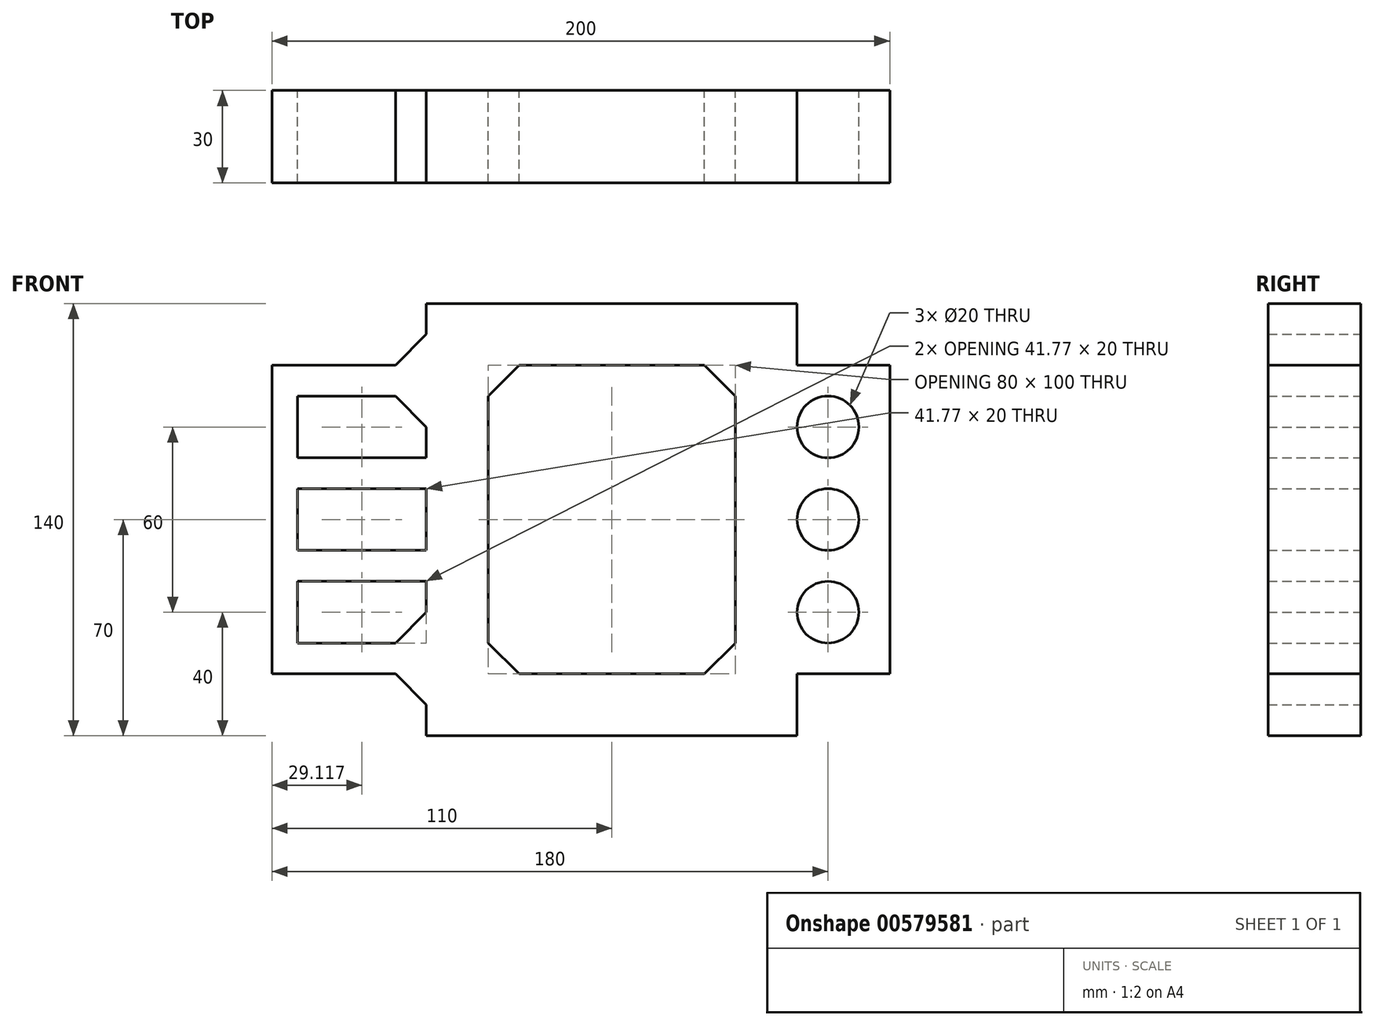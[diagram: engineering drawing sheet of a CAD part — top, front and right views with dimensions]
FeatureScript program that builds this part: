
annotation { "Feature Type Name" : "Feature", "Feature Type Description" : "" }
export const myFeature = defineFeature(function(context is Context, id is Id, definition is map)
    precondition{}
    {
        {
            var Q0;
            Q0=qCreatedBy(makeId("Front.planeOp"),FACE);
            var sketch = newSketch(context, id + "F0", { "sketchPlane" : qUnion([Q0])});
            skLineSegment(sketch, "E0", {"start": v(0, 0) * mm, "end": v(120, 0) * mm});
            skLineSegment(sketch, "E1", {"start": v(120, 0) * mm, "end": v(120, 20) * mm});
            skLineSegment(sketch, "E2", {"start": v(120, 20) * mm, "end": v(150, 20) * mm});
            skLineSegment(sketch, "E3", {"start": v(150, 20) * mm, "end": v(150, 120) * mm});
            skLineSegment(sketch, "E4", {"start": v(150, 120) * mm, "end": v(120, 120) * mm});
            skLineSegment(sketch, "E5", {"start": v(120, 120) * mm, "end": v(120, 140) * mm});
            skLineSegment(sketch, "E6", {"start": v(120, 140) * mm, "end": v(0, 140) * mm});
            skLineSegment(sketch, "E7", {"start": v(0, 140) * mm, "end": v(0, 130) * mm});
            skLineSegment(sketch, "E8", {"start": v(-19.49, 120) * mm, "end": v(-50, 120) * mm});
            skLineSegment(sketch, "E9", {"start": v(-50, 120) * mm, "end": v(-50, 20) * mm});
            skLineSegment(sketch, "E10", {"start": v(-50, 20) * mm, "end": v(-19.49, 20) * mm});
            skLineSegment(sketch, "E11", {"start": v(0, 10) * mm, "end": v(0, 0) * mm});
            skLineSegment(sketch, "E12", {"start": v(-19.49, 120) * mm, "end": v(-10, 120) * mm});
            skLineSegment(sketch, "E13", {"start": v(0, 130) * mm, "end": v(0, 140) * mm});
            skLineSegment(sketch, "E14", {"start": v(30, 120) * mm, "end": v(90, 120) * mm});
            skLineSegment(sketch, "E15", {"start": v(100, 110) * mm, "end": v(100, 30) * mm});
            skLineSegment(sketch, "E16", {"start": v(90, 20) * mm, "end": v(30, 20) * mm});
            skLineSegment(sketch, "E17", {"start": v(20, 30) * mm, "end": v(20, 110) * mm});
            skPoint(sketch, "E18.visualSharp", {"position": v(0, 120) * mm});
            skLineSegment(sketch, "E19", {"start": v(-10, 120) * mm, "end": v(0, 130) * mm});
            skPoint(sketch, "E20.visualSharp", {"position": v(0, 41.92) * mm});
            skLineSegment(sketch, "E21", {"start": v(-19.49, 20) * mm, "end": v(-10, 20) * mm});
            skLineSegment(sketch, "E22", {"start": v(0, 10) * mm, "end": v(0, 10) * mm});
            skPoint(sketch, "E23.visualSharp", {"position": v(0, 20) * mm});
            skLineSegment(sketch, "E24", {"start": v(-10, 20) * mm, "end": v(0, 10) * mm});
            skLineSegment(sketch, "E25", {"start": v(60, 20) * mm, "end": v(60, 0) * mm, "construction": true});
            skPoint(sketch, "E26.visualSharp", {"position": v(20, 120) * mm});
            skPoint(sketch, "E27.visualSharp", {"position": v(100, 120) * mm});
            skPoint(sketch, "E28.visualSharp", {"position": v(100, 20) * mm});
            skPoint(sketch, "E29.visualSharp", {"position": v(20, 20) * mm});
            skLineSegment(sketch, "E30", {"start": v(20, 110) * mm, "end": v(30, 120) * mm});
            skLineSegment(sketch, "E31", {"start": v(90, 120) * mm, "end": v(100, 110) * mm});
            skLineSegment(sketch, "E32", {"start": v(100, 30) * mm, "end": v(90, 20) * mm});
            skLineSegment(sketch, "E33", {"start": v(30, 20) * mm, "end": v(20, 30) * mm});
            skLineSegment(sketch, "E34.bottom", {"start": v(-41.77, 110) * mm, "end": v(-10, 110) * mm});
            skLineSegment(sketch, "E34.top", {"start": v(-41.77, 90) * mm, "end": v(0, 90) * mm});
            skLineSegment(sketch, "E34.left", {"start": v(-41.77, 110) * mm, "end": v(-41.77, 90) * mm});
            skLineSegment(sketch, "E34.right", {"start": v(0, 100) * mm, "end": v(0, 90) * mm});
            skLineSegment(sketch, "E35.bottom", {"start": v(-41.77, 80) * mm, "end": v(0, 80) * mm});
            skLineSegment(sketch, "E35.top", {"start": v(-41.77, 60) * mm, "end": v(0, 60) * mm});
            skLineSegment(sketch, "E35.left", {"start": v(-41.77, 80) * mm, "end": v(-41.77, 60) * mm});
            skLineSegment(sketch, "E35.right", {"start": v(0, 80) * mm, "end": v(0, 60) * mm});
            skLineSegment(sketch, "E36.bottom", {"start": v(-41.77, 50) * mm, "end": v(0, 50) * mm});
            skLineSegment(sketch, "E36.top", {"start": v(-41.77, 30) * mm, "end": v(-10, 30) * mm});
            skLineSegment(sketch, "E36.left", {"start": v(-41.77, 50) * mm, "end": v(-41.77, 30) * mm});
            skLineSegment(sketch, "E36.right", {"start": v(0, 50) * mm, "end": v(0, 40) * mm});
            skCircle(sketch, "E37", {"center": v(130, 100) * mm, "radius": 10 * mm});
            skCircle(sketch, "E38", {"center": v(130, 70) * mm, "radius": 10 * mm});
            skCircle(sketch, "E39", {"center": v(130, 40) * mm, "radius": 10 * mm});
            skPoint(sketch, "E40.visualSharp", {"position": v(0, 110) * mm});
            skPoint(sketch, "E41.visualSharp", {"position": v(0, 30) * mm});
            skLineSegment(sketch, "E42", {"start": v(0, 100) * mm, "end": v(-10, 110) * mm});
            skLineSegment(sketch, "E43", {"start": v(-10, 30) * mm, "end": v(0, 40) * mm});
            skSolve(sketch);
        }
        {
            var Q0;
            Q0=qSketchRegion(id+"F0",true);
            extrude(context, id + "F1", {"entities" : qUnion([Q0]), "depth" : 30 * mm, "offsetDistance" : 25 * mm});
        }
    });
